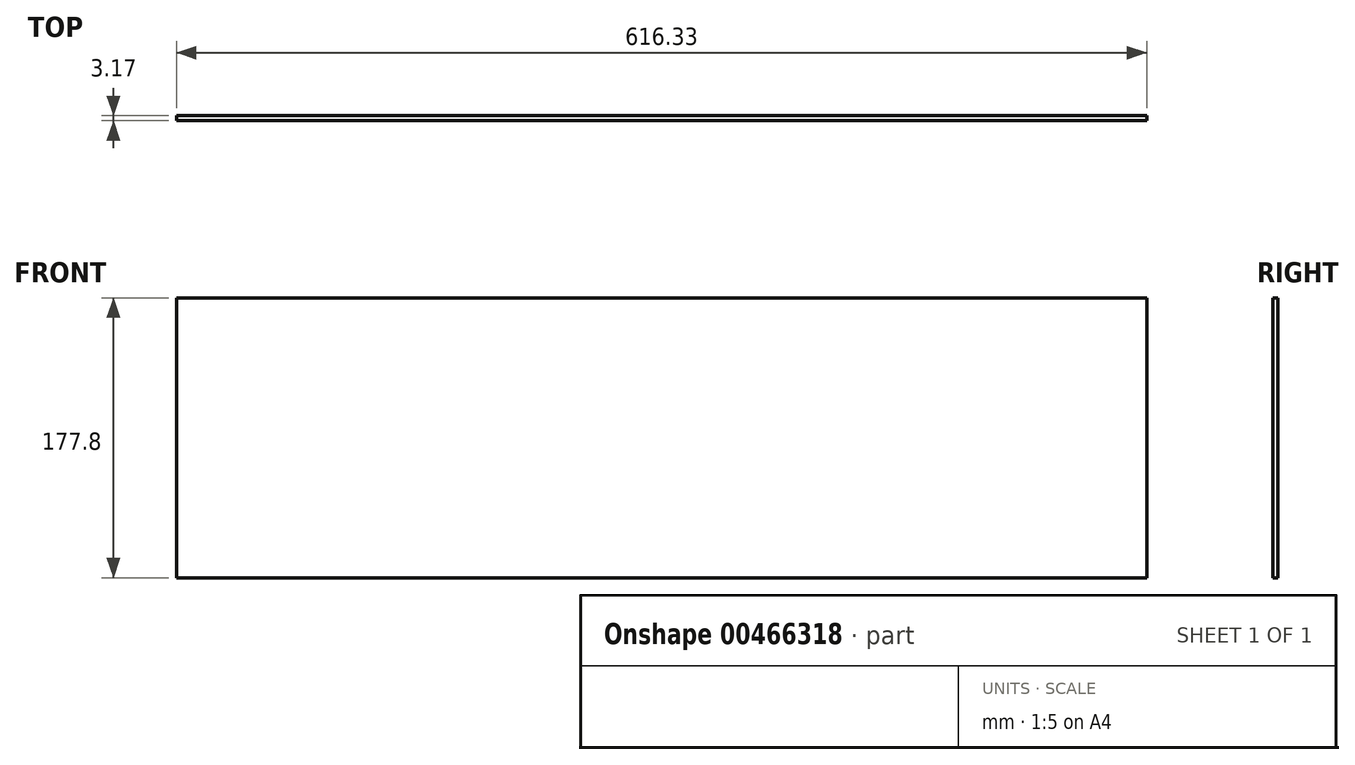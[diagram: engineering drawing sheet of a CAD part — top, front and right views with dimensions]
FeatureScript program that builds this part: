
annotation { "Feature Type Name" : "Feature", "Feature Type Description" : "" }
export const myFeature = defineFeature(function(context is Context, id is Id, definition is map)
    precondition{}
    {
        {
            var Q0;
            Q0=qCreatedBy(makeId("Front.planeOp"),FACE);
            var sketch = newSketch(context, id + "F0", { "sketchPlane" : qUnion([Q0])});
            skLineSegment(sketch, "E0.bottom", {"start": v(-384.34, -151.47) * mm, "end": v(231.99, -151.47) * mm});
            skLineSegment(sketch, "E0.top", {"start": v(-384.34, -329.27) * mm, "end": v(231.99, -329.27) * mm});
            skLineSegment(sketch, "E0.left", {"start": v(-384.34, -151.47) * mm, "end": v(-384.34, -329.27) * mm});
            skLineSegment(sketch, "E0.right", {"start": v(231.99, -151.47) * mm, "end": v(231.99, -329.27) * mm});
            skSolve(sketch);
        }
        {
            var Q0;
            Q0 = qSketchRegion(id + "F0", true);
            extrude(context, id + "F1", {"entities" : qUnion([Q0]), "depth" : 3.17 * mm});
        }
    });
